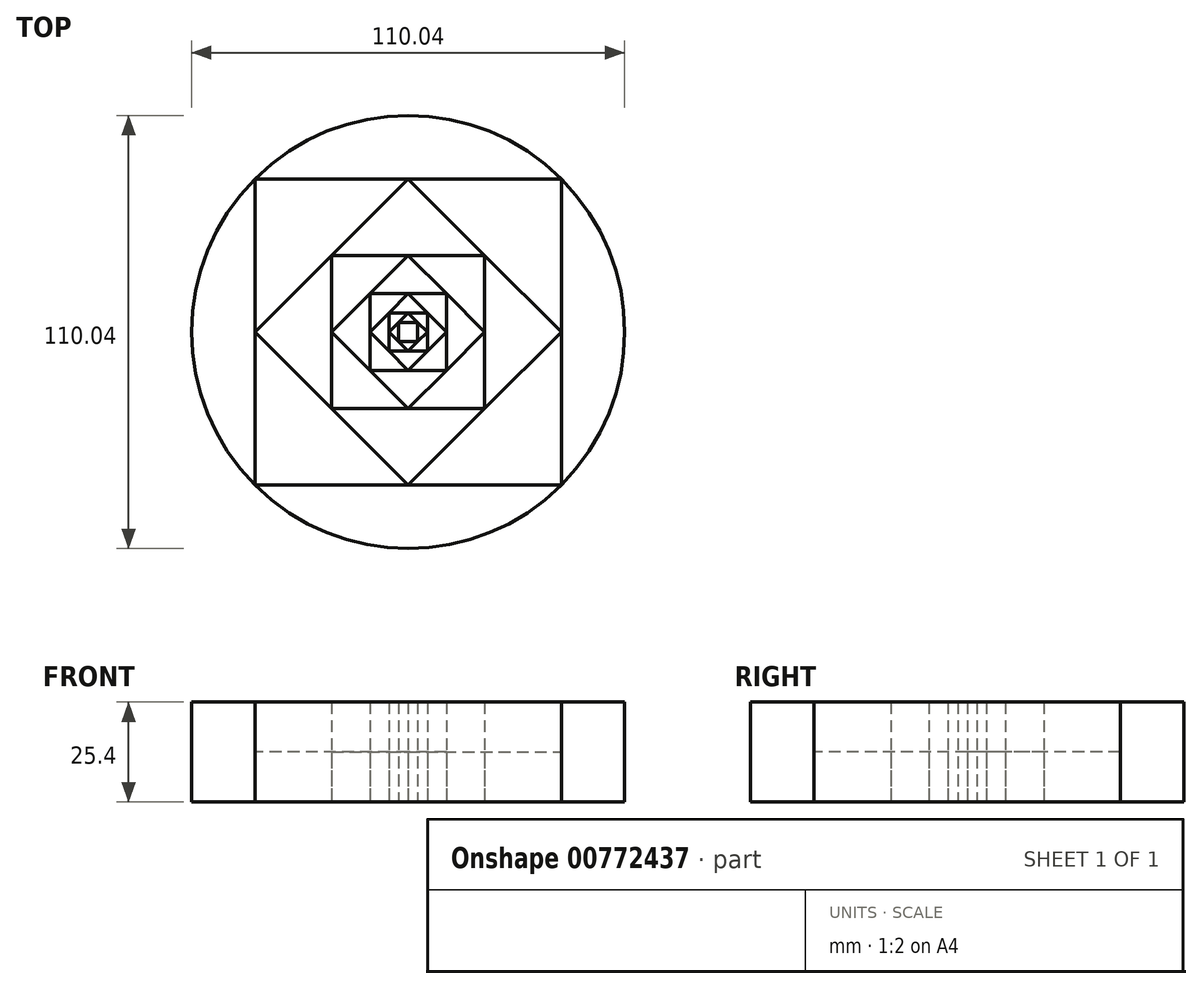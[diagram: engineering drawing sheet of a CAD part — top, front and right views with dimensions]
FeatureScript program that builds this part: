
annotation { "Feature Type Name" : "Feature", "Feature Type Description" : "" }
export const myFeature = defineFeature(function(context is Context, id is Id, definition is map)
    precondition{}
    {
        {
            var Q0;
            Q0=qCreatedBy(makeId("Top.planeOp"),FACE);
            var sketch = newSketch(context, id + "F0", { "sketchPlane" : qUnion([Q0])});
            skLineSegment(sketch, "E0", {"start": v(0, 77.8) * mm, "end": v(-77.8, 0) * mm});
            skLineSegment(sketch, "E1", {"start": v(-77.8, 0) * mm, "end": v(0, -77.8) * mm});
            skLineSegment(sketch, "E2", {"start": v(0, -77.8) * mm, "end": v(77.8, 0) * mm});
            skLineSegment(sketch, "E3", {"start": v(77.8, 0) * mm, "end": v(0, 77.8) * mm});
            skLineSegment(sketch, "E4", {"start": v(-38.9, 38.9) * mm, "end": v(-38.9, -38.9) * mm});
            skLineSegment(sketch, "E5", {"start": v(-38.9, -38.9) * mm, "end": v(38.9, -38.9) * mm});
            skLineSegment(sketch, "E6", {"start": v(38.9, -38.9) * mm, "end": v(38.9, 38.9) * mm});
            skLineSegment(sketch, "E7", {"start": v(38.9, 38.9) * mm, "end": v(-38.9, 38.9) * mm});
            skLineSegment(sketch, "E8", {"start": v(0, 38.9) * mm, "end": v(-38.9, 0) * mm});
            skLineSegment(sketch, "E9", {"start": v(-38.9, 0) * mm, "end": v(0, -38.9) * mm});
            skLineSegment(sketch, "E10", {"start": v(0, -38.9) * mm, "end": v(38.9, 0) * mm});
            skLineSegment(sketch, "E11", {"start": v(38.9, 0) * mm, "end": v(0, 38.9) * mm});
            skLineSegment(sketch, "E12", {"start": v(-19.45, 19.45) * mm, "end": v(-19.45, -19.45) * mm});
            skLineSegment(sketch, "E13", {"start": v(-19.45, -19.45) * mm, "end": v(19.45, -19.45) * mm});
            skLineSegment(sketch, "E14", {"start": v(19.45, -19.45) * mm, "end": v(19.45, 19.45) * mm});
            skLineSegment(sketch, "E15", {"start": v(19.45, 19.45) * mm, "end": v(-19.45, 19.45) * mm});
            skLineSegment(sketch, "E16", {"start": v(0, 19.45) * mm, "end": v(-19.45, 0) * mm});
            skLineSegment(sketch, "E17", {"start": v(-19.45, 0) * mm, "end": v(0, -19.45) * mm});
            skLineSegment(sketch, "E18", {"start": v(0, -19.45) * mm, "end": v(19.45, 0) * mm});
            skLineSegment(sketch, "E19", {"start": v(19.45, 0) * mm, "end": v(0, 19.45) * mm});
            skLineSegment(sketch, "E20", {"start": v(9.73, 9.73) * mm, "end": v(-9.73, 9.73) * mm});
            skLineSegment(sketch, "E21", {"start": v(-9.73, 9.73) * mm, "end": v(-9.73, -9.73) * mm});
            skLineSegment(sketch, "E22", {"start": v(-9.73, -9.73) * mm, "end": v(9.73, -9.73) * mm});
            skLineSegment(sketch, "E23", {"start": v(9.73, -9.73) * mm, "end": v(9.73, 9.73) * mm});
            skLineSegment(sketch, "E24", {"start": v(0, 9.73) * mm, "end": v(-9.73, 0) * mm});
            skLineSegment(sketch, "E25", {"start": v(-9.73, 0) * mm, "end": v(0, -9.73) * mm});
            skLineSegment(sketch, "E26", {"start": v(0, -9.73) * mm, "end": v(9.73, 0) * mm});
            skLineSegment(sketch, "E27", {"start": v(9.73, 0) * mm, "end": v(0, 9.73) * mm});
            skLineSegment(sketch, "E28", {"start": v(-4.86, 4.86) * mm, "end": v(-4.86, -4.86) * mm});
            skLineSegment(sketch, "E29", {"start": v(-4.86, -4.86) * mm, "end": v(4.86, -4.86) * mm});
            skLineSegment(sketch, "E30", {"start": v(4.86, -4.86) * mm, "end": v(4.86, 4.86) * mm});
            skLineSegment(sketch, "E31", {"start": v(4.86, 4.86) * mm, "end": v(-4.86, 4.86) * mm});
            skLineSegment(sketch, "E32", {"start": v(0, 4.86) * mm, "end": v(-4.86, 0) * mm});
            skLineSegment(sketch, "E33", {"start": v(-4.86, 0) * mm, "end": v(0, -4.86) * mm});
            skLineSegment(sketch, "E34", {"start": v(0, -4.86) * mm, "end": v(4.86, 0) * mm});
            skLineSegment(sketch, "E35", {"start": v(4.86, 0) * mm, "end": v(0, 4.86) * mm});
            skLineSegment(sketch, "E36", {"start": v(-2.43, 2.43) * mm, "end": v(-2.43, -2.43) * mm});
            skLineSegment(sketch, "E37", {"start": v(-2.43, -2.43) * mm, "end": v(2.43, -2.43) * mm});
            skLineSegment(sketch, "E38", {"start": v(2.43, -2.43) * mm, "end": v(2.43, 2.43) * mm});
            skLineSegment(sketch, "E39", {"start": v(2.43, 2.43) * mm, "end": v(-2.43, 2.43) * mm});
            skSolve(sketch);
        }
        {
            var Q0;
            {var subQ0=sQuery(id+"F0.wireOp",EDGE,"E3");var subQ1=sQuery(id+"F0.wireOp",EDGE,"E0");var subQ2=makeQuery(id+"F0.imprint","INTERSECT",VERTEX,{"derivedFrom":[subQ1,subQ0]});Q0=makeQuery(id+"F0.imprint","IMPRINT",FACE,{"disambiguationData":[TD([[makeQuery(id+"F0.imprint","IMPRINT",EDGE,{"disambiguationData":[TD([[subQ2,-1.0]])],"derivedFrom":subQ1}),1.0]])]});}
            var Q1;
            {var subQ0=sQuery(id+"F0.wireOp",EDGE,"E1");var subQ1=sQuery(id+"F0.wireOp",EDGE,"E0");var subQ2=makeQuery(id+"F0.imprint","INTERSECT",VERTEX,{"derivedFrom":[subQ1,subQ0]});Q1=makeQuery(id+"F0.imprint","IMPRINT",FACE,{"disambiguationData":[TD([[makeQuery(id+"F0.imprint","IMPRINT",EDGE,{"disambiguationData":[TD([[subQ2,1.0]])],"derivedFrom":subQ1}),1.0]])]});}
            var Q2;
            {var subQ0=sQuery(id+"F0.wireOp",EDGE,"E2");var subQ1=sQuery(id+"F0.wireOp",EDGE,"E1");var subQ2=makeQuery(id+"F0.imprint","INTERSECT",VERTEX,{"derivedFrom":[subQ1,subQ0]});Q2=makeQuery(id+"F0.imprint","IMPRINT",FACE,{"disambiguationData":[TD([[makeQuery(id+"F0.imprint","IMPRINT",EDGE,{"disambiguationData":[TD([[subQ2,1.0]])],"derivedFrom":subQ1}),1.0]])]});}
            var Q3;
            {var subQ0=sQuery(id+"F0.wireOp",EDGE,"E3");var subQ1=sQuery(id+"F0.wireOp",EDGE,"E2");var subQ2=makeQuery(id+"F0.imprint","INTERSECT",VERTEX,{"derivedFrom":[subQ1,subQ0]});Q3=makeQuery(id+"F0.imprint","IMPRINT",FACE,{"disambiguationData":[TD([[makeQuery(id+"F0.imprint","IMPRINT",EDGE,{"disambiguationData":[TD([[subQ2,1.0]])],"derivedFrom":subQ1}),1.0]])]});}
            extrude(context, id + "F1", {"entities" : qUnion([Q0, Q1, Q2, Q3]), "depth" : 25.4 * mm, "offsetDistance" : 25.4 * mm});
        }
        {
            var Q0;
            {var subQ0=sQuery(id+"F0.wireOp",EDGE,"E7");var subQ1=sQuery(id+"F0.wireOp",EDGE,"E4");var subQ2=makeQuery(id+"F0.imprint","INTERSECT",VERTEX,{"derivedFrom":[sQuery(id+"F0.wireOp",EDGE,"E0"),subQ1,subQ0]});Q0=makeQuery(id+"F0.imprint","IMPRINT",FACE,{"disambiguationData":[TD([[makeQuery(id+"F0.imprint","IMPRINT",EDGE,{"disambiguationData":[TD([[subQ2,-1.0]])],"derivedFrom":subQ1}),1.0]])]});}
            var Q1;
            {var subQ0=sQuery(id+"F0.wireOp",EDGE,"E5");var subQ1=sQuery(id+"F0.wireOp",EDGE,"E4");var subQ2=makeQuery(id+"F0.imprint","INTERSECT",VERTEX,{"derivedFrom":[sQuery(id+"F0.wireOp",EDGE,"E1"),subQ1,subQ0]});Q1=makeQuery(id+"F0.imprint","IMPRINT",FACE,{"disambiguationData":[TD([[makeQuery(id+"F0.imprint","IMPRINT",EDGE,{"disambiguationData":[TD([[subQ2,1.0]])],"derivedFrom":subQ1}),1.0]])]});}
            var Q2;
            {var subQ0=sQuery(id+"F0.wireOp",EDGE,"E6");var subQ1=sQuery(id+"F0.wireOp",EDGE,"E5");var subQ2=makeQuery(id+"F0.imprint","INTERSECT",VERTEX,{"derivedFrom":[sQuery(id+"F0.wireOp",EDGE,"E2"),subQ1,subQ0]});Q2=makeQuery(id+"F0.imprint","IMPRINT",FACE,{"disambiguationData":[TD([[makeQuery(id+"F0.imprint","IMPRINT",EDGE,{"disambiguationData":[TD([[subQ2,1.0]])],"derivedFrom":subQ1}),1.0]])]});}
            var Q3;
            {var subQ0=sQuery(id+"F0.wireOp",EDGE,"E7");var subQ1=sQuery(id+"F0.wireOp",EDGE,"E6");var subQ2=makeQuery(id+"F0.imprint","INTERSECT",VERTEX,{"derivedFrom":[sQuery(id+"F0.wireOp",EDGE,"E3"),subQ1,subQ0]});Q3=makeQuery(id+"F0.imprint","IMPRINT",FACE,{"disambiguationData":[TD([[makeQuery(id+"F0.imprint","IMPRINT",EDGE,{"disambiguationData":[TD([[subQ2,1.0]])],"derivedFrom":subQ1}),1.0]])]});}
            extrude(context, id + "F2", {"entities" : qUnion([Q0, Q1, Q2, Q3]), "depth" : 12.7 * mm, "offsetDistance" : 25.4 * mm});
        }
        {
            var Q0;
            {var subQ0=sQuery(id+"F0.wireOp",EDGE,"E11");var subQ1=sQuery(id+"F0.wireOp",EDGE,"E8");var subQ2=makeQuery(id+"F0.imprint","INTERSECT",VERTEX,{"derivedFrom":[sQuery(id+"F0.wireOp",EDGE,"E7"),subQ1,subQ0]});Q0=makeQuery(id+"F0.imprint","IMPRINT",FACE,{"disambiguationData":[TD([[makeQuery(id+"F0.imprint","IMPRINT",EDGE,{"disambiguationData":[TD([[subQ2,-1.0]])],"derivedFrom":subQ1}),1.0]])]});}
            var Q1;
            {var subQ0=sQuery(id+"F0.wireOp",EDGE,"E9");var subQ1=sQuery(id+"F0.wireOp",EDGE,"E8");var subQ2=makeQuery(id+"F0.imprint","INTERSECT",VERTEX,{"derivedFrom":[sQuery(id+"F0.wireOp",EDGE,"E4"),subQ1,subQ0]});Q1=makeQuery(id+"F0.imprint","IMPRINT",FACE,{"disambiguationData":[TD([[makeQuery(id+"F0.imprint","IMPRINT",EDGE,{"disambiguationData":[TD([[subQ2,1.0]])],"derivedFrom":subQ1}),1.0]])]});}
            var Q2;
            {var subQ0=sQuery(id+"F0.wireOp",EDGE,"E11");var subQ1=sQuery(id+"F0.wireOp",EDGE,"E10");var subQ2=makeQuery(id+"F0.imprint","INTERSECT",VERTEX,{"derivedFrom":[sQuery(id+"F0.wireOp",EDGE,"E6"),subQ1,subQ0]});Q2=makeQuery(id+"F0.imprint","IMPRINT",FACE,{"disambiguationData":[TD([[makeQuery(id+"F0.imprint","IMPRINT",EDGE,{"disambiguationData":[TD([[subQ2,1.0]])],"derivedFrom":subQ1}),1.0]])]});}
            var Q3;
            {var subQ0=sQuery(id+"F0.wireOp",EDGE,"E10");var subQ1=sQuery(id+"F0.wireOp",EDGE,"E9");var subQ2=makeQuery(id+"F0.imprint","INTERSECT",VERTEX,{"derivedFrom":[sQuery(id+"F0.wireOp",EDGE,"E5"),subQ1,subQ0]});Q3=makeQuery(id+"F0.imprint","IMPRINT",FACE,{"disambiguationData":[TD([[makeQuery(id+"F0.imprint","IMPRINT",EDGE,{"disambiguationData":[TD([[subQ2,1.0]])],"derivedFrom":subQ1}),1.0]])]});}
            extrude(context, id + "F3", {"entities" : qUnion([Q0, Q1, Q2, Q3]), "depth" : 25.4 * mm, "offsetDistance" : 25.4 * mm});
        }
        {
            var Q0;
            {var subQ0=sQuery(id+"F0.wireOp",EDGE,"E15");var subQ1=sQuery(id+"F0.wireOp",EDGE,"E12");var subQ2=makeQuery(id+"F0.imprint","INTERSECT",VERTEX,{"derivedFrom":[sQuery(id+"F0.wireOp",EDGE,"E8"),subQ1,subQ0]});Q0=makeQuery(id+"F0.imprint","IMPRINT",FACE,{"disambiguationData":[TD([[makeQuery(id+"F0.imprint","IMPRINT",EDGE,{"disambiguationData":[TD([[subQ2,-1.0]])],"derivedFrom":subQ1}),1.0]])]});}
            var Q1;
            {var subQ0=sQuery(id+"F0.wireOp",EDGE,"E13");var subQ1=sQuery(id+"F0.wireOp",EDGE,"E12");var subQ2=makeQuery(id+"F0.imprint","INTERSECT",VERTEX,{"derivedFrom":[sQuery(id+"F0.wireOp",EDGE,"E9"),subQ1,subQ0]});Q1=makeQuery(id+"F0.imprint","IMPRINT",FACE,{"disambiguationData":[TD([[makeQuery(id+"F0.imprint","IMPRINT",EDGE,{"disambiguationData":[TD([[subQ2,1.0]])],"derivedFrom":subQ1}),1.0]])]});}
            var Q2;
            {var subQ0=sQuery(id+"F0.wireOp",EDGE,"E14");var subQ1=sQuery(id+"F0.wireOp",EDGE,"E13");var subQ2=makeQuery(id+"F0.imprint","INTERSECT",VERTEX,{"derivedFrom":[sQuery(id+"F0.wireOp",EDGE,"E10"),subQ1,subQ0]});Q2=makeQuery(id+"F0.imprint","IMPRINT",FACE,{"disambiguationData":[TD([[makeQuery(id+"F0.imprint","IMPRINT",EDGE,{"disambiguationData":[TD([[subQ2,1.0]])],"derivedFrom":subQ1}),1.0]])]});}
            var Q3;
            {var subQ0=sQuery(id+"F0.wireOp",EDGE,"E15");var subQ1=sQuery(id+"F0.wireOp",EDGE,"E14");var subQ2=makeQuery(id+"F0.imprint","INTERSECT",VERTEX,{"derivedFrom":[sQuery(id+"F0.wireOp",EDGE,"E11"),subQ1,subQ0]});Q3=makeQuery(id+"F0.imprint","IMPRINT",FACE,{"disambiguationData":[TD([[makeQuery(id+"F0.imprint","IMPRINT",EDGE,{"disambiguationData":[TD([[subQ2,1.0]])],"derivedFrom":subQ1}),1.0]])]});}
            extrude(context, id + "F4", {"entities" : qUnion([Q0, Q1, Q2, Q3]), "depth" : 12.7 * mm, "offsetDistance" : 25.4 * mm});
        }
        {
            var Q0;
            {var subQ0=sQuery(id+"F0.wireOp",EDGE,"E19");var subQ1=sQuery(id+"F0.wireOp",EDGE,"E16");var subQ2=makeQuery(id+"F0.imprint","INTERSECT",VERTEX,{"derivedFrom":[sQuery(id+"F0.wireOp",EDGE,"E15"),subQ1,subQ0]});Q0=makeQuery(id+"F0.imprint","IMPRINT",FACE,{"disambiguationData":[TD([[makeQuery(id+"F0.imprint","IMPRINT",EDGE,{"disambiguationData":[TD([[subQ2,-1.0]])],"derivedFrom":subQ1}),1.0]])]});}
            var Q1;
            {var subQ0=sQuery(id+"F0.wireOp",EDGE,"E17");var subQ1=sQuery(id+"F0.wireOp",EDGE,"E16");var subQ2=makeQuery(id+"F0.imprint","INTERSECT",VERTEX,{"derivedFrom":[sQuery(id+"F0.wireOp",EDGE,"E12"),subQ1,subQ0]});Q1=makeQuery(id+"F0.imprint","IMPRINT",FACE,{"disambiguationData":[TD([[makeQuery(id+"F0.imprint","IMPRINT",EDGE,{"disambiguationData":[TD([[subQ2,1.0]])],"derivedFrom":subQ1}),1.0]])]});}
            var Q2;
            {var subQ0=sQuery(id+"F0.wireOp",EDGE,"E19");var subQ1=sQuery(id+"F0.wireOp",EDGE,"E18");var subQ2=makeQuery(id+"F0.imprint","INTERSECT",VERTEX,{"derivedFrom":[sQuery(id+"F0.wireOp",EDGE,"E14"),subQ1,subQ0]});Q2=makeQuery(id+"F0.imprint","IMPRINT",FACE,{"disambiguationData":[TD([[makeQuery(id+"F0.imprint","IMPRINT",EDGE,{"disambiguationData":[TD([[subQ2,1.0]])],"derivedFrom":subQ1}),1.0]])]});}
            var Q3;
            {var subQ0=sQuery(id+"F0.wireOp",EDGE,"E18");var subQ1=sQuery(id+"F0.wireOp",EDGE,"E17");var subQ2=makeQuery(id+"F0.imprint","INTERSECT",VERTEX,{"derivedFrom":[sQuery(id+"F0.wireOp",EDGE,"E13"),subQ1,subQ0]});Q3=makeQuery(id+"F0.imprint","IMPRINT",FACE,{"disambiguationData":[TD([[makeQuery(id+"F0.imprint","IMPRINT",EDGE,{"disambiguationData":[TD([[subQ2,1.0]])],"derivedFrom":subQ1}),1.0]])]});}
            extrude(context, id + "F5", {"entities" : qUnion([Q0, Q1, Q2, Q3]), "depth" : 25.4 * mm, "offsetDistance" : 25.4 * mm});
        }
        {
            var Q0;
            {var subQ0=sQuery(id+"F0.wireOp",EDGE,"E21");var subQ1=sQuery(id+"F0.wireOp",EDGE,"E20");var subQ2=makeQuery(id+"F0.imprint","INTERSECT",VERTEX,{"derivedFrom":[sQuery(id+"F0.wireOp",EDGE,"E16"),subQ1,subQ0]});Q0=makeQuery(id+"F0.imprint","IMPRINT",FACE,{"disambiguationData":[TD([[makeQuery(id+"F0.imprint","IMPRINT",EDGE,{"disambiguationData":[TD([[subQ2,1.0]])],"derivedFrom":subQ1}),1.0]])]});}
            var Q1;
            {var subQ0=sQuery(id+"F0.wireOp",EDGE,"E22");var subQ1=sQuery(id+"F0.wireOp",EDGE,"E21");var subQ2=makeQuery(id+"F0.imprint","INTERSECT",VERTEX,{"derivedFrom":[sQuery(id+"F0.wireOp",EDGE,"E17"),subQ1,subQ0]});Q1=makeQuery(id+"F0.imprint","IMPRINT",FACE,{"disambiguationData":[TD([[makeQuery(id+"F0.imprint","IMPRINT",EDGE,{"disambiguationData":[TD([[subQ2,1.0]])],"derivedFrom":subQ1}),1.0]])]});}
            var Q2;
            {var subQ0=sQuery(id+"F0.wireOp",EDGE,"E23");var subQ1=sQuery(id+"F0.wireOp",EDGE,"E22");var subQ2=makeQuery(id+"F0.imprint","INTERSECT",VERTEX,{"derivedFrom":[sQuery(id+"F0.wireOp",EDGE,"E18"),subQ1,subQ0]});Q2=makeQuery(id+"F0.imprint","IMPRINT",FACE,{"disambiguationData":[TD([[makeQuery(id+"F0.imprint","IMPRINT",EDGE,{"disambiguationData":[TD([[subQ2,1.0]])],"derivedFrom":subQ1}),1.0]])]});}
            var Q3;
            {var subQ0=sQuery(id+"F0.wireOp",EDGE,"E23");var subQ1=sQuery(id+"F0.wireOp",EDGE,"E20");var subQ2=makeQuery(id+"F0.imprint","INTERSECT",VERTEX,{"derivedFrom":[sQuery(id+"F0.wireOp",EDGE,"E19"),subQ1,subQ0]});Q3=makeQuery(id+"F0.imprint","IMPRINT",FACE,{"disambiguationData":[TD([[makeQuery(id+"F0.imprint","IMPRINT",EDGE,{"disambiguationData":[TD([[subQ2,-1.0]])],"derivedFrom":subQ1}),1.0]])]});}
            extrude(context, id + "F6", {"entities" : qUnion([Q0, Q1, Q2, Q3]), "depth" : 12.7 * mm, "offsetDistance" : 25.4 * mm});
        }
        {
            var Q0;
            {var subQ0=sQuery(id+"F0.wireOp",EDGE,"E27");var subQ1=sQuery(id+"F0.wireOp",EDGE,"E24");var subQ2=makeQuery(id+"F0.imprint","INTERSECT",VERTEX,{"derivedFrom":[sQuery(id+"F0.wireOp",EDGE,"E20"),subQ1,subQ0]});Q0=makeQuery(id+"F0.imprint","IMPRINT",FACE,{"disambiguationData":[TD([[makeQuery(id+"F0.imprint","IMPRINT",EDGE,{"disambiguationData":[TD([[subQ2,-1.0]])],"derivedFrom":subQ1}),1.0]])]});}
            var Q1;
            {var subQ0=sQuery(id+"F0.wireOp",EDGE,"E25");var subQ1=sQuery(id+"F0.wireOp",EDGE,"E24");var subQ2=makeQuery(id+"F0.imprint","INTERSECT",VERTEX,{"derivedFrom":[sQuery(id+"F0.wireOp",EDGE,"E21"),subQ1,subQ0]});Q1=makeQuery(id+"F0.imprint","IMPRINT",FACE,{"disambiguationData":[TD([[makeQuery(id+"F0.imprint","IMPRINT",EDGE,{"disambiguationData":[TD([[subQ2,1.0]])],"derivedFrom":subQ1}),1.0]])]});}
            var Q2;
            {var subQ0=sQuery(id+"F0.wireOp",EDGE,"E26");var subQ1=sQuery(id+"F0.wireOp",EDGE,"E25");var subQ2=makeQuery(id+"F0.imprint","INTERSECT",VERTEX,{"derivedFrom":[sQuery(id+"F0.wireOp",EDGE,"E22"),subQ1,subQ0]});Q2=makeQuery(id+"F0.imprint","IMPRINT",FACE,{"disambiguationData":[TD([[makeQuery(id+"F0.imprint","IMPRINT",EDGE,{"disambiguationData":[TD([[subQ2,1.0]])],"derivedFrom":subQ1}),1.0]])]});}
            var Q3;
            {var subQ0=sQuery(id+"F0.wireOp",EDGE,"E27");var subQ1=sQuery(id+"F0.wireOp",EDGE,"E26");var subQ2=makeQuery(id+"F0.imprint","INTERSECT",VERTEX,{"derivedFrom":[sQuery(id+"F0.wireOp",EDGE,"E23"),subQ1,subQ0]});Q3=makeQuery(id+"F0.imprint","IMPRINT",FACE,{"disambiguationData":[TD([[makeQuery(id+"F0.imprint","IMPRINT",EDGE,{"disambiguationData":[TD([[subQ2,1.0]])],"derivedFrom":subQ1}),1.0]])]});}
            extrude(context, id + "F7", {"entities" : qUnion([Q0, Q1, Q2, Q3]), "depth" : 25.4 * mm, "offsetDistance" : 25.4 * mm});
        }
        {
            var Q0;
            {var subQ0=sQuery(id+"F0.wireOp",EDGE,"E31");var subQ1=sQuery(id+"F0.wireOp",EDGE,"E28");var subQ2=makeQuery(id+"F0.imprint","INTERSECT",VERTEX,{"derivedFrom":[sQuery(id+"F0.wireOp",EDGE,"E24"),subQ1,subQ0]});Q0=makeQuery(id+"F0.imprint","IMPRINT",FACE,{"disambiguationData":[TD([[makeQuery(id+"F0.imprint","IMPRINT",EDGE,{"disambiguationData":[TD([[subQ2,-1.0]])],"derivedFrom":subQ1}),1.0]])]});}
            var Q1;
            {var subQ0=sQuery(id+"F0.wireOp",EDGE,"E29");var subQ1=sQuery(id+"F0.wireOp",EDGE,"E28");var subQ2=makeQuery(id+"F0.imprint","INTERSECT",VERTEX,{"derivedFrom":[sQuery(id+"F0.wireOp",EDGE,"E25"),subQ1,subQ0]});Q1=makeQuery(id+"F0.imprint","IMPRINT",FACE,{"disambiguationData":[TD([[makeQuery(id+"F0.imprint","IMPRINT",EDGE,{"disambiguationData":[TD([[subQ2,1.0]])],"derivedFrom":subQ1}),1.0]])]});}
            var Q2;
            {var subQ0=sQuery(id+"F0.wireOp",EDGE,"E30");var subQ1=sQuery(id+"F0.wireOp",EDGE,"E29");var subQ2=makeQuery(id+"F0.imprint","INTERSECT",VERTEX,{"derivedFrom":[sQuery(id+"F0.wireOp",EDGE,"E26"),subQ1,subQ0]});Q2=makeQuery(id+"F0.imprint","IMPRINT",FACE,{"disambiguationData":[TD([[makeQuery(id+"F0.imprint","IMPRINT",EDGE,{"disambiguationData":[TD([[subQ2,1.0]])],"derivedFrom":subQ1}),1.0]])]});}
            var Q3;
            {var subQ0=sQuery(id+"F0.wireOp",EDGE,"E31");var subQ1=sQuery(id+"F0.wireOp",EDGE,"E30");var subQ2=makeQuery(id+"F0.imprint","INTERSECT",VERTEX,{"derivedFrom":[sQuery(id+"F0.wireOp",EDGE,"E27"),subQ1,subQ0]});Q3=makeQuery(id+"F0.imprint","IMPRINT",FACE,{"disambiguationData":[TD([[makeQuery(id+"F0.imprint","IMPRINT",EDGE,{"disambiguationData":[TD([[subQ2,1.0]])],"derivedFrom":subQ1}),1.0]])]});}
            extrude(context, id + "F8", {"entities" : qUnion([Q0, Q1, Q2, Q3]), "depth" : 12.7 * mm, "offsetDistance" : 25.4 * mm});
        }
        {
            var Q0;
            {var subQ3=sQuery(id+"F0.wireOp",EDGE,"E39");Q0=makeQuery(id+"F0.imprint","IMPRINT",FACE,{"disambiguationData":[TD([[makeQuery(id+"F0.imprint","IMPRINT",EDGE,{"derivedFrom":subQ3}),-1.0]])]});}
            var Q1;
            {var subQ3=sQuery(id+"F0.wireOp",EDGE,"E36");Q1=makeQuery(id+"F0.imprint","IMPRINT",FACE,{"disambiguationData":[TD([[makeQuery(id+"F0.imprint","IMPRINT",EDGE,{"derivedFrom":subQ3}),-1.0]])]});}
            var Q2;
            {var subQ3=sQuery(id+"F0.wireOp",EDGE,"E37");Q2=makeQuery(id+"F0.imprint","IMPRINT",FACE,{"disambiguationData":[TD([[makeQuery(id+"F0.imprint","IMPRINT",EDGE,{"derivedFrom":subQ3}),-1.0]])]});}
            var Q3;
            {var subQ3=sQuery(id+"F0.wireOp",EDGE,"E38");Q3=makeQuery(id+"F0.imprint","IMPRINT",FACE,{"disambiguationData":[TD([[makeQuery(id+"F0.imprint","IMPRINT",EDGE,{"derivedFrom":subQ3}),-1.0]])]});}
            extrude(context, id + "F9", {"entities" : qUnion([Q0, Q1, Q2, Q3]), "depth" : 25.4 * mm, "offsetDistance" : 25.4 * mm});
        }
        {
            var Q0;
            Q0=makeQuery(id+"F1.opExtrude","CAP_FACE",FACE,{"disambiguationData":[OSD([sQuery(id+"F0.wireOp",EDGE,"E0"),sQuery(id+"F0.wireOp",EDGE,"E1"),sQuery(id+"F0.wireOp",EDGE,"E4")])],"isStart":true});
            var sketch = newSketch(context, id + "F10", { "sketchPlane" : qUnion([Q0])});
            skCircle(sketch, "E40", {"center": v(0, 0) * mm, "radius": 55.02 * mm});
            skSolve(sketch);
        }
        {
            var Q0;
            {var subQ1=sQuery(id+"F0.wireOp",EDGE,"E4");var subQ2=makeQuery(id+"F1.opExtrude","CAP_EDGE",EDGE,{"disambiguationData":[OSD([subQ1])],"isStart":true});Q0=makeQuery(id+"F10.imprint","IMPRINT",FACE,{"disambiguationData":[TD([[makeQuery(id+"F10.imprint","IMPRINT",EDGE,{"derivedFrom":subQ2}),1.0]])]});}
            var Q1;
            {var subQ1=sQuery(id+"F0.wireOp",EDGE,"E4");var subQ2=makeQuery(id+"F1.opExtrude","CAP_EDGE",EDGE,{"disambiguationData":[OSD([subQ1])],"isStart":true});Q1=makeQuery(id+"F10.imprint","IMPRINT",FACE,{"disambiguationData":[TD([[makeQuery(id+"F10.imprint","IMPRINT",EDGE,{"derivedFrom":subQ2}),-1.0]])]});}
            extrude(context, id + "F11", {"entities" : qUnion([Q0, Q1]), "operationType" : NewBodyOperationType.INTERSECT, "oppositeDirection" : true, "depth" : 77.9 * mm, "offsetDistance" : 25 * mm});
        }
    });
